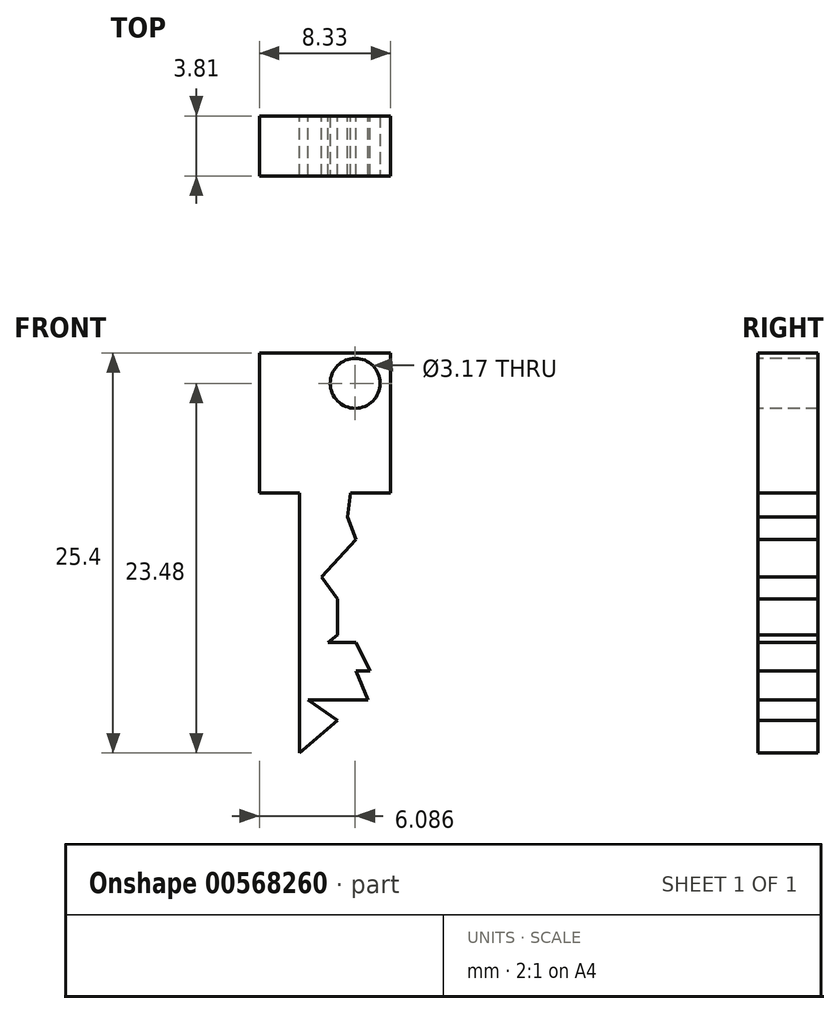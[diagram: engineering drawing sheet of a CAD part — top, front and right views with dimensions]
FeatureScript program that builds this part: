
annotation { "Feature Type Name" : "Feature", "Feature Type Description" : "" }
export const myFeature = defineFeature(function(context is Context, id is Id, definition is map)
    precondition{}
    {
        {
            var Q0;
            Q0=qCreatedBy(makeId("Front.planeOp"),FACE);
            var sketch = newSketch(context, id + "F0", { "sketchPlane" : qUnion([Q0])});
            skLineSegment(sketch, "E0.bottom", {"start": v(0, 0) * mm, "end": v(25.4, 0) * mm});
            skLineSegment(sketch, "E0.top", {"start": v(0, 25.4) * mm, "end": v(25.4, 25.4) * mm});
            skLineSegment(sketch, "E0.left", {"start": v(0, 0) * mm, "end": v(0, 25.4) * mm});
            skLineSegment(sketch, "E0.right", {"start": v(25.4, 0) * mm, "end": v(25.4, 25.4) * mm});
            skSolve(sketch);
        }
        {
            var Q0;
            Q0 = qSketchRegion(id + "F0", true);
            extrude(context, id + "F1", {"entities" : qUnion([Q0]), "depth" : 25.4 * mm, "offsetDistance" : 25.4 * mm});
        }
        {
            var Q0;
            Q0=qCreatedBy(makeId("Front.planeOp"),FACE);
            cPlane(context, id + "F2", {"entities" : qUnion([Q0]), "cplaneType" : CPlaneType.OFFSET, "offset" : 25.4 * mm, "width" : 152.4 * mm, "height" : 152.4 * mm});
        }
        {
            var Q0;
            Q0=qCreatedBy(id+"F2.planeOp",FACE);
            var sketch = newSketch(context, id + "F3", { "sketchPlane" : qUnion([Q0])});
            skLineSegment(sketch, "E1", {"start": v(7.65, 25.4) * mm, "end": v(7.65, 16.5) * mm});
            skLineSegment(sketch, "E2", {"start": v(7.65, 16.51) * mm, "end": v(10.2, 16.51) * mm});
            skLineSegment(sketch, "E3", {"start": v(13.44, 16.51) * mm, "end": v(15.98, 16.51) * mm});
            skLineSegment(sketch, "E4", {"start": v(15.98, 16.51) * mm, "end": v(15.98, 25.4) * mm});
            skLineSegment(sketch, "E5", {"start": v(10.2, 16.5) * mm, "end": v(10.2, 0) * mm});
            skLineSegment(sketch, "E6", {"start": v(10.2, 0) * mm, "end": v(12.6, 2.06) * mm});
            skLineSegment(sketch, "E7", {"start": v(12.6, 2.06) * mm, "end": v(10.74, 3.37) * mm});
            skLineSegment(sketch, "E8", {"start": v(10.74, 3.37) * mm, "end": v(14.55, 3.37) * mm});
            skLineSegment(sketch, "E9", {"start": v(14.55, 3.37) * mm, "end": v(13.8, 5.2) * mm});
            skLineSegment(sketch, "E10", {"start": v(13.8, 5.2) * mm, "end": v(14.68, 5.2) * mm});
            skLineSegment(sketch, "E11", {"start": v(14.68, 5.2) * mm, "end": v(13.8, 7.02) * mm});
            skLineSegment(sketch, "E12", {"start": v(13.8, 7.02) * mm, "end": v(12.02, 7.02) * mm});
            skLineSegment(sketch, "E13", {"start": v(12.02, 7.02) * mm, "end": v(12.6, 7.5) * mm});
            skLineSegment(sketch, "E14", {"start": v(12.6, 7.5) * mm, "end": v(12.6, 9.79) * mm});
            skLineSegment(sketch, "E15", {"start": v(12.6, 9.79) * mm, "end": v(11.59, 11.18) * mm});
            skLineSegment(sketch, "E16", {"start": v(11.59, 11.18) * mm, "end": v(13.8, 13.57) * mm});
            skLineSegment(sketch, "E17", {"start": v(13.8, 13.57) * mm, "end": v(13.25, 15) * mm});
            skLineSegment(sketch, "E18", {"start": v(13.25, 15) * mm, "end": v(13.44, 16.51) * mm});
            skLineSegment(sketch, "E19", {"start": v(15.98, 25.4) * mm, "end": v(7.65, 25.4) * mm});
            skSolve(sketch);
        }
        {
            var Q0;
            Q0=makeQuery(id+"F1.opExtrude","SWEPT_FACE",FACE,{"disambiguationData":[OSD([sQuery(id+"F0.wireOp",EDGE,"E0.top")])]});
            extrude(context, id + "F4", {"entities" : qUnion([Q0]), "operationType" : NewBodyOperationType.REMOVE, "oppositeDirection" : true, "depth" : 25.4 * mm, "offsetDistance" : 25.4 * mm});
        }
        {
            var Q0;
            Q0=makeQuery(id+"F3.imprint","IMPRINT",FACE,{"disambiguationData":[TD([[makeQuery(id+"F3.imprint","IMPRINT",EDGE,{"derivedFrom":sQuery(id+"F3.wireOp",EDGE,"E1")}),1.0]])]});
            extrude(context, id + "F5", {"entities" : qUnion([Q0]), "depth" : 3.8 * mm, "offsetDistance" : 25.4 * mm});
        }
        {
            var Q0;
            Q0=makeQuery(id+"F5.opExtrude","CAP_FACE",FACE,{"disambiguationData":[OSD([sQuery(id+"F3.wireOp",EDGE,"E1"),sQuery(id+"F3.wireOp",EDGE,"E2"),sQuery(id+"F3.wireOp",EDGE,"E3"),sQuery(id+"F3.wireOp",EDGE,"E4"),sQuery(id+"F3.wireOp",EDGE,"E5"),sQuery(id+"F3.wireOp",EDGE,"E6"),sQuery(id+"F3.wireOp",EDGE,"E7"),sQuery(id+"F3.wireOp",EDGE,"E8"),sQuery(id+"F3.wireOp",EDGE,"E9"),sQuery(id+"F3.wireOp",EDGE,"E10"),sQuery(id+"F3.wireOp",EDGE,"E11"),sQuery(id+"F3.wireOp",EDGE,"E12"),sQuery(id+"F3.wireOp",EDGE,"E13"),sQuery(id+"F3.wireOp",EDGE,"E14"),sQuery(id+"F3.wireOp",EDGE,"E15"),sQuery(id+"F3.wireOp",EDGE,"E16"),sQuery(id+"F3.wireOp",EDGE,"E17"),sQuery(id+"F3.wireOp",EDGE,"E18"),sQuery(id+"F3.wireOp",EDGE,"E19")])],"isStart":false});
            var sketch = newSketch(context, id + "F6", { "sketchPlane" : qUnion([Q0])});
            skCircle(sketch, "E20", {"center": v(13.74, 23.48) * mm, "radius": 1.59 * mm});
            skSolve(sketch);
        }
        {
            var Q0;
            Q0 = qSketchRegion(id + "F6", true);
            extrude(context, id + "F7", {"entities" : qUnion([Q0]), "operationType" : NewBodyOperationType.REMOVE, "oppositeDirection" : true, "depth" : 25.4 * mm, "offsetDistance" : 25.4 * mm});
        }
    });
